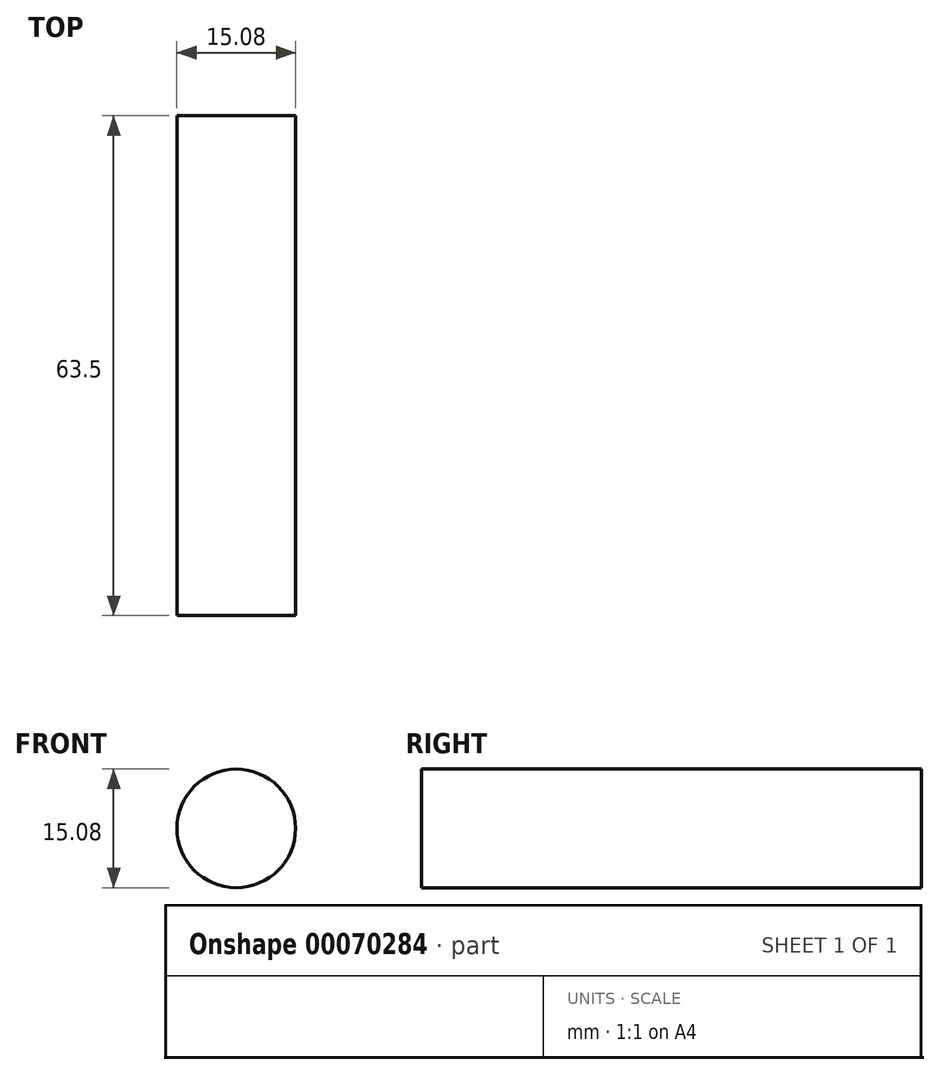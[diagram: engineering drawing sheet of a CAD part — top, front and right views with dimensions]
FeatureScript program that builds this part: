
annotation { "Feature Type Name" : "Feature", "Feature Type Description" : "" }
export const myFeature = defineFeature(function(context is Context, id is Id, definition is map)
    precondition{}
    {
        {
            var Q0;
            Q0=qCreatedBy(makeId("Front.planeOp"),FACE);
            var sketch = newSketch(context, id + "F0", { "sketchPlane" : qUnion([Q0])});
            skCircle(sketch, "E0", {"center": v(0, 0) * mm, "radius": 7.54 * mm});
            skSolve(sketch);
        }
        {
            var Q0;
            Q0=makeQuery(id+"F0.imprint","IMPRINT",FACE,{"disambiguationData":[TD([[makeQuery(id+"F0.imprint","IMPRINT",EDGE,{"derivedFrom":sQuery(id+"F0.wireOp",EDGE,"E0")}),1.0]])]});
            extrude(context, id + "F1", {"entities" : qUnion([Q0]), "depth" : 63.5 * mm});
        }
    });
